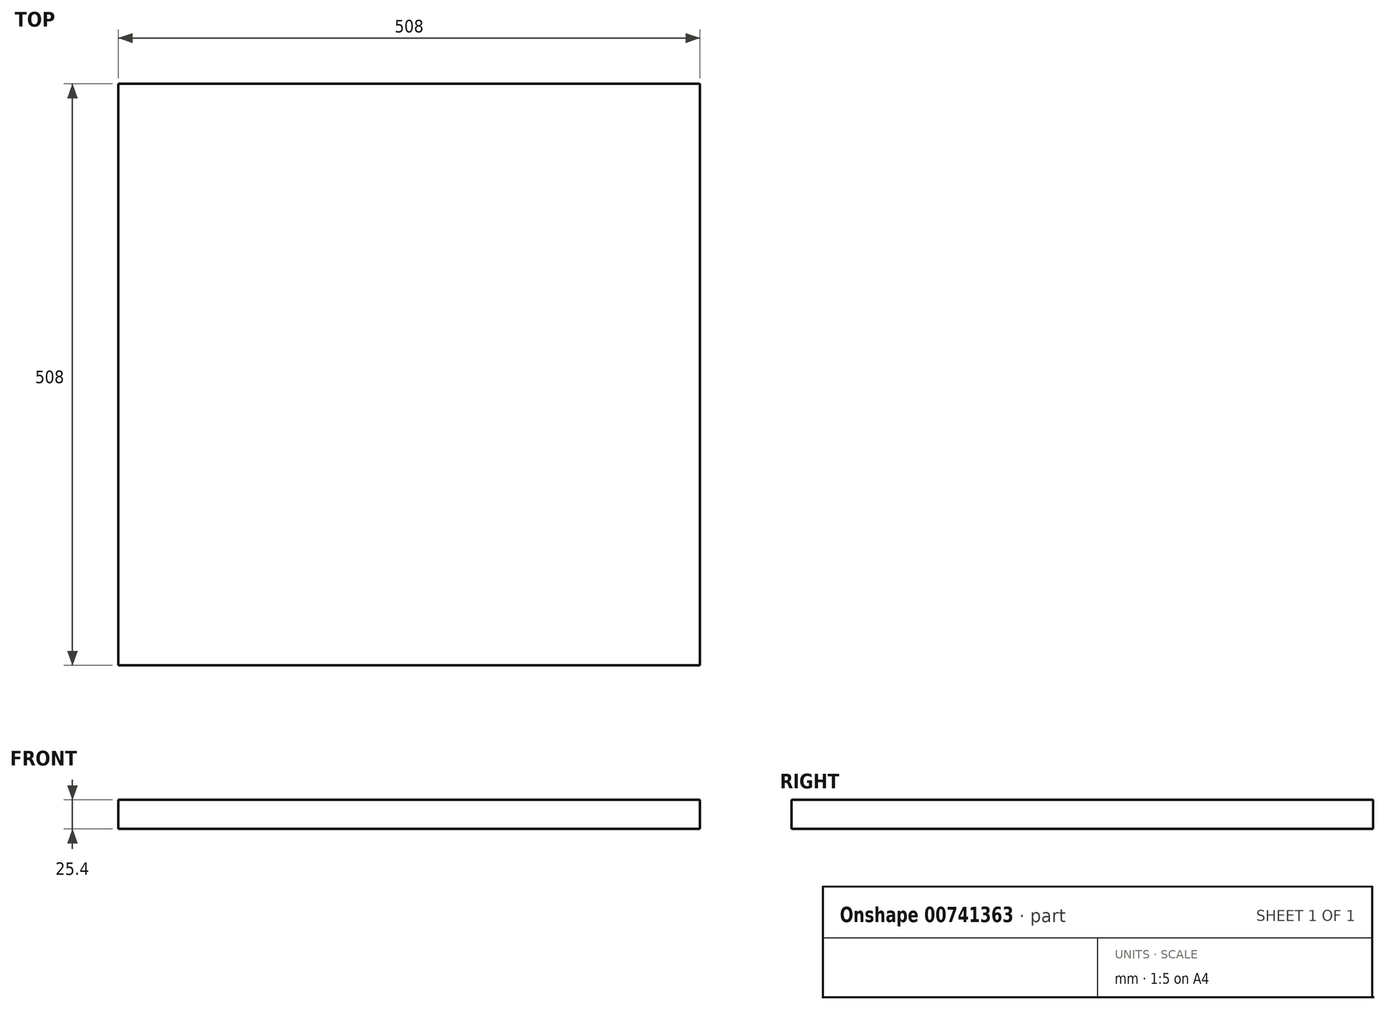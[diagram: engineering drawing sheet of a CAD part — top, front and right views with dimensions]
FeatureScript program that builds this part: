
annotation { "Feature Type Name" : "Feature", "Feature Type Description" : "" }
export const myFeature = defineFeature(function(context is Context, id is Id, definition is map)
    precondition{}
    {
        {
            var Q0;
            Q0=qCreatedBy(makeId("Top.planeOp"),FACE);
            var sketch = newSketch(context, id + "F0", { "sketchPlane" : qUnion([Q0])});
            skLineSegment(sketch, "E0.bottom", {"start": v(-254, 254) * mm, "end": v(254, 254) * mm});
            skLineSegment(sketch, "E0.top", {"start": v(-254, -254) * mm, "end": v(254, -254) * mm});
            skLineSegment(sketch, "E0.left", {"start": v(-254, 254) * mm, "end": v(-254, -254) * mm});
            skLineSegment(sketch, "E0.right", {"start": v(254, 254) * mm, "end": v(254, -254) * mm});
            skPoint(sketch, "E0.middle", {"position": v(0, 0) * mm});
            skSolve(sketch);
        }
        {
            var Q0;
            Q0=makeQuery(id+"F0.imprint","IMPRINT",FACE,{"disambiguationData":[TD([[makeQuery(id+"F0.imprint","IMPRINT",EDGE,{"derivedFrom":sQuery(id+"F0.wireOp",EDGE,"E0.bottom")}),-1.0]])]});
            extrude(context, id + "F1", {"entities" : qUnion([Q0]), "depth" : 25.4 * mm, "offsetDistance" : 25.4 * mm});
        }
    });
